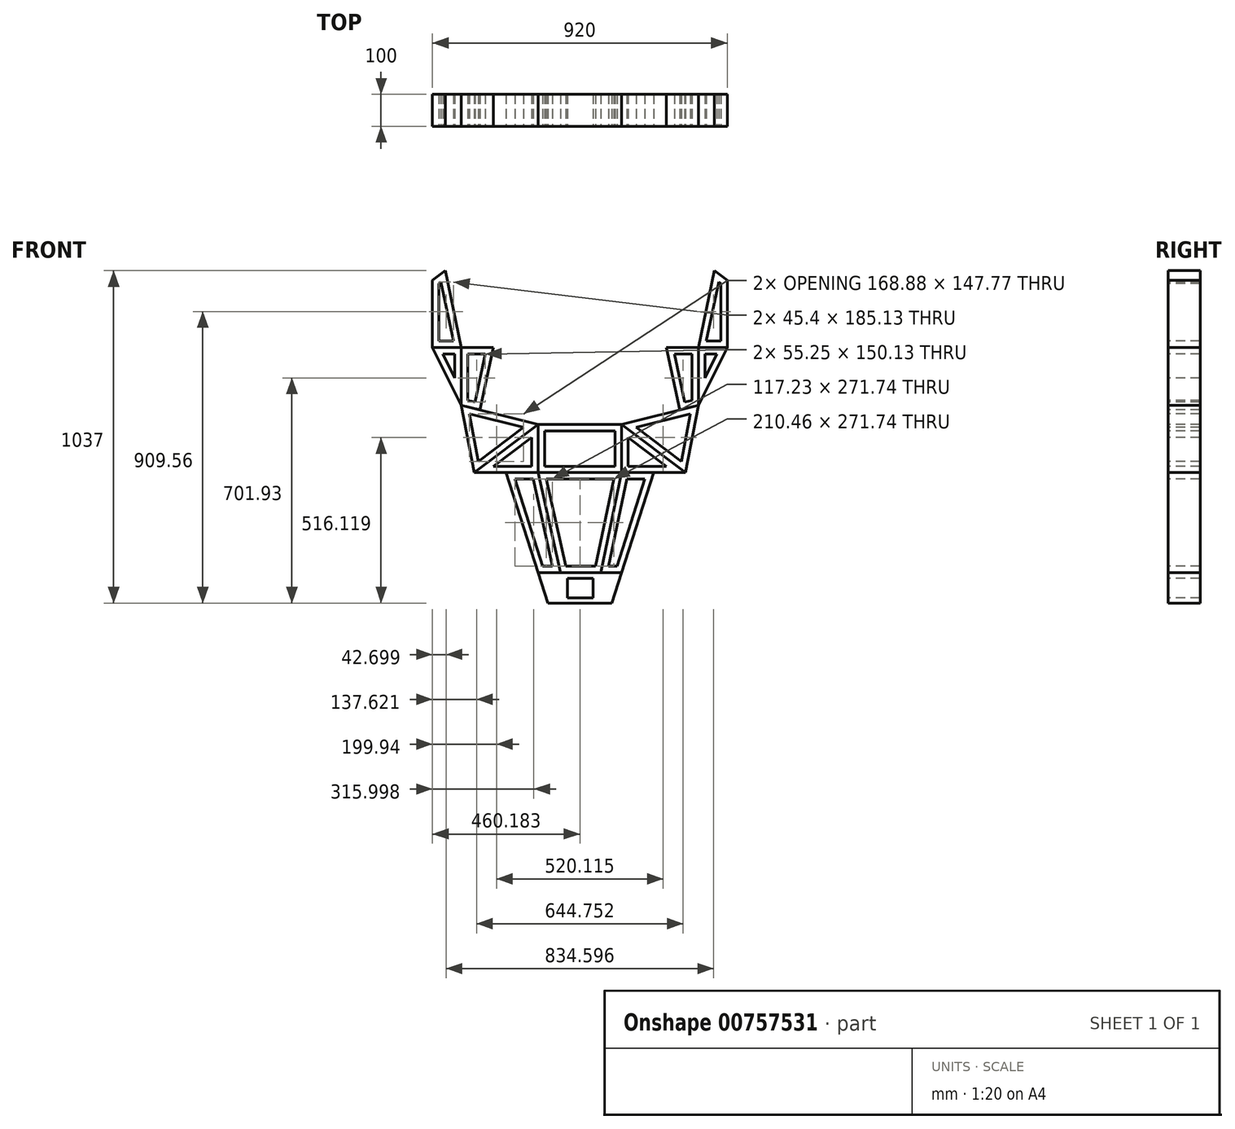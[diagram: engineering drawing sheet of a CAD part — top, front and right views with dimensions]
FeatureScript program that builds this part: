
annotation { "Feature Type Name" : "Feature", "Feature Type Description" : "" }
export const myFeature = defineFeature(function(context is Context, id is Id, definition is map)
    precondition{}
    {
        {
            var Q0;
            Q0=qCreatedBy(makeId("Top.planeOp"),FACE);
            cPlane(context, id + "F0", {"entities" : qUnion([Q0]), "cplaneType" : CPlaneType.OFFSET, "offset" : 526 * mm, "width" : 150 * mm, "height" : 150 * mm});
        }
        {
            var Q0;
            Q0=qCreatedBy(makeId("Front.planeOp"),FACE);
            var sketch = newSketch(context, id + "F1", { "sketchPlane" : qUnion([Q0])});
            skLineSegment(sketch, "E0", {"start": v(-220.81, -516.5) * mm, "end": v(-120.81, -516.5) * mm});
            skLineSegment(sketch, "E1", {"start": v(-350.81, -109.5) * mm, "end": v(-220.81, -516.5) * mm});
            skLineSegment(sketch, "E2", {"start": v(-350.81, -109.5) * mm, "end": v(-450.81, -109.5) * mm});
            skLineSegment(sketch, "E3", {"start": v(-490.81, 100.5) * mm, "end": v(-450.81, -109.5) * mm});
            skLineSegment(sketch, "E4", {"start": v(-580.81, 280.5) * mm, "end": v(-490.81, 100.5) * mm});
            skLineSegment(sketch, "E5", {"start": v(-580.81, 280.5) * mm, "end": v(-580.81, 490.5) * mm});
            skLineSegment(sketch, "E6", {"start": v(-540.81, 520.5) * mm, "end": v(-580.81, 490.5) * mm});
            skLineSegment(sketch, "E7", {"start": v(-580.81, 280.5) * mm, "end": v(-490.81, 280.5) * mm});
            skLineSegment(sketch, "E8", {"start": v(-490.81, 280.5) * mm, "end": v(-390.81, 280.5) * mm});
            skLineSegment(sketch, "E9", {"start": v(-540.81, 520.5) * mm, "end": v(-490.81, 280.5) * mm});
            skLineSegment(sketch, "E10", {"start": v(-490.81, 280.5) * mm, "end": v(-490.81, 100.5) * mm});
            skLineSegment(sketch, "E11", {"start": v(-250.81, 40.5) * mm, "end": v(-490.81, 100.5) * mm});
            skLineSegment(sketch, "E12", {"start": v(-250.81, 40.5) * mm, "end": v(-250.81, -109.5) * mm});
            skLineSegment(sketch, "E13", {"start": v(-250.81, -109.5) * mm, "end": v(-450.81, -109.5) * mm});
            skLineSegment(sketch, "E14", {"start": v(-250.81, 40.5) * mm, "end": v(-450.81, -109.5) * mm});
            skLineSegment(sketch, "E15", {"start": v(-490.81, 100.5) * mm, "end": v(-432.6, 85.95) * mm});
            skLineSegment(sketch, "E16", {"start": v(-432.6, 85.95) * mm, "end": v(-390.81, 280.5) * mm});
            skLineSegment(sketch, "E17", {"start": v(-250.81, 40.5) * mm, "end": v(-120.81, 40.5) * mm});
            skLineSegment(sketch, "E18", {"start": v(-237.82, -109.5) * mm, "end": v(-120.81, -109.5) * mm});
            skLineSegment(sketch, "E19", {"start": v(-220.81, -516.5) * mm, "end": v(-251.24, -421.23) * mm});
            skLineSegment(sketch, "E20", {"start": v(-251.24, -421.23) * mm, "end": v(-120.81, -421.23) * mm});
            skLineSegment(sketch, "E21.MirrorCS", {"start": v(249.19, 100.5) * mm, "end": v(190.98, 85.95) * mm});
            skLineSegment(sketch, "E22.MirrorCS", {"start": v(190.98, 85.95) * mm, "end": v(149.19, 280.5) * mm});
            skLineSegment(sketch, "E23.MirrorCS", {"start": v(-20.81, -516.5) * mm, "end": v(9.61, -421.23) * mm});
            skLineSegment(sketch, "E24.MirrorCS", {"start": v(9.19, 40.5) * mm, "end": v(9.19, -109.5) * mm});
            skLineSegment(sketch, "E25.MirrorCS", {"start": v(9.19, 40.5) * mm, "end": v(249.19, 100.5) * mm});
            skLineSegment(sketch, "E26.MirrorCS", {"start": v(9.19, 40.5) * mm, "end": v(209.19, -109.5) * mm});
            skLineSegment(sketch, "E27.MirrorCS", {"start": v(9.19, -109.5) * mm, "end": v(209.19, -109.5) * mm});
            skLineSegment(sketch, "E28.MirrorCS", {"start": v(109.19, -109.5) * mm, "end": v(209.19, -109.5) * mm});
            skLineSegment(sketch, "E29.MirrorCS", {"start": v(109.19, -109.5) * mm, "end": v(-20.81, -516.5) * mm});
            skLineSegment(sketch, "E30.MirrorCS", {"start": v(299.19, 520.5) * mm, "end": v(249.19, 280.5) * mm});
            skLineSegment(sketch, "E31.MirrorCS", {"start": v(339.19, 280.5) * mm, "end": v(249.19, 100.5) * mm});
            skLineSegment(sketch, "E32.MirrorCS", {"start": v(249.19, 280.5) * mm, "end": v(149.19, 280.5) * mm});
            skLineSegment(sketch, "E33.MirrorCS", {"start": v(299.19, 520.5) * mm, "end": v(339.19, 490.5) * mm});
            skLineSegment(sketch, "E34.MirrorCS", {"start": v(249.19, 280.5) * mm, "end": v(249.19, 100.5) * mm});
            skLineSegment(sketch, "E35.MirrorCS", {"start": v(339.19, 280.5) * mm, "end": v(339.19, 490.5) * mm});
            skLineSegment(sketch, "E36.MirrorCS", {"start": v(249.19, 100.5) * mm, "end": v(209.19, -109.5) * mm});
            skLineSegment(sketch, "E37.MirrorCS", {"start": v(339.19, 280.5) * mm, "end": v(249.19, 280.5) * mm});
            skLineSegment(sketch, "E38", {"start": v(-120.81, -516.5) * mm, "end": v(-20.81, -516.5) * mm});
            skLineSegment(sketch, "E39", {"start": v(-120.81, -109.5) * mm, "end": v(9.19, -109.5) * mm});
            skLineSegment(sketch, "E40", {"start": v(9.19, 40.5) * mm, "end": v(-120.81, 40.5) * mm});
            skLineSegment(sketch, "E41", {"start": v(-237.82, -109.5) * mm, "end": v(-250.81, -109.5) * mm});
            skLineSegment(sketch, "E42", {"start": v(-120.81, -421.23) * mm, "end": v(9.61, -421.23) * mm});
            skLineSegment(sketch, "E43", {"start": v(-251.24, -421.23) * mm, "end": v(-181.24, -421.23) * mm});
            skLineSegment(sketch, "E44", {"start": v(-181.24, -421.23) * mm, "end": v(-250.81, -109.5) * mm});
            skLineSegment(sketch, "E45", {"start": v(9.61, -421.23) * mm, "end": v(-55.6, -421.23) * mm});
            skLineSegment(sketch, "E46", {"start": v(9.19, -109.5) * mm, "end": v(-55.6, -421.23) * mm});
            skLineSegment(sketch, "E47.bottom", {"start": v(-160, -439.9) * mm, "end": v(-80, -439.9) * mm});
            skLineSegment(sketch, "E47.top", {"start": v(-160, -499.9) * mm, "end": v(-80, -499.9) * mm});
            skLineSegment(sketch, "E47.left", {"start": v(-160, -439.9) * mm, "end": v(-160, -499.9) * mm});
            skLineSegment(sketch, "E47.right", {"start": v(-80, -439.9) * mm, "end": v(-80, -499.9) * mm});
            skSolve(sketch);
        }
        {
            var Q0;
            Q0=makeQuery(id+"F1.imprint","IMPRINT",FACE,{"disambiguationData":[TD([[makeQuery(id+"F1.imprint","IMPRINT",EDGE,{"derivedFrom":sQuery(id+"F1.wireOp",EDGE,"E5")}),-1.0]])]});
            var Q1;
            Q1=makeQuery(id+"F1.imprint","IMPRINT",FACE,{"disambiguationData":[TD([[makeQuery(id+"F1.imprint","IMPRINT",EDGE,{"derivedFrom":sQuery(id+"F1.wireOp",EDGE,"E8")}),-1.0]])]});
            var Q2;
            {var subQ0=sQuery(id+"F1.wireOp",EDGE,"E12");Q2=makeQuery(id+"F1.imprint","IMPRINT",FACE,{"disambiguationData":[TD([[makeQuery(id+"F1.imprint","IMPRINT",EDGE,{"derivedFrom":subQ0}),-1.0]])]});}
            var Q3;
            {var subQ2=sQuery(id+"F1.wireOp",EDGE,"E26.MirrorCS");Q3=makeQuery(id+"F1.imprint","IMPRINT",FACE,{"disambiguationData":[TD([[makeQuery(id+"F1.imprint","IMPRINT",EDGE,{"derivedFrom":subQ2}),1.0]])]});}
            var Q4;
            Q4=makeQuery(id+"F1.imprint","IMPRINT",FACE,{"disambiguationData":[TD([[makeQuery(id+"F1.imprint","IMPRINT",EDGE,{"derivedFrom":sQuery(id+"F1.wireOp",EDGE,"E31.MirrorCS")}),-1.0]])]});
            var Q5;
            {var subQ1=sQuery(id+"F1.wireOp",EDGE,"E18");Q5=makeQuery(id+"F1.imprint","IMPRINT",FACE,{"disambiguationData":[TD([[makeQuery(id+"F1.imprint","IMPRINT",EDGE,{"derivedFrom":subQ1}),-1.0]])]});}
            extrude(context, id + "F2", {"entities" : qUnion([Q0, Q1, Q2, Q3, Q4, Q5]), "oppositeDirection" : true, "depth" : 100 * mm, "offsetDistance" : 25 * mm});
        }
        {
            var Q0;
            Q0=makeQuery(id+"F2.opExtrude","CAP_FACE",FACE,{"disambiguationData":[OSD([sQuery(id+"F1.wireOp",EDGE,"E5"),sQuery(id+"F1.wireOp",EDGE,"E6"),sQuery(id+"F1.wireOp",EDGE,"E7"),sQuery(id+"F1.wireOp",EDGE,"E9")])],"isStart":false});
            var Q1;
            Q1=makeQuery(id+"F2.opExtrude","CAP_FACE",FACE,{"disambiguationData":[OSD([sQuery(id+"F1.wireOp",EDGE,"E8"),sQuery(id+"F1.wireOp",EDGE,"E10"),sQuery(id+"F1.wireOp",EDGE,"E15"),sQuery(id+"F1.wireOp",EDGE,"E16")])],"isStart":false});
            var Q2;
            Q2=makeQuery(id+"F2.opExtrude","CAP_FACE",FACE,{"disambiguationData":[OSD([sQuery(id+"F1.wireOp",EDGE,"E5"),sQuery(id+"F1.wireOp",EDGE,"E6"),sQuery(id+"F1.wireOp",EDGE,"E7"),sQuery(id+"F1.wireOp",EDGE,"E9")])],"isStart":true});
            var Q3;
            Q3=makeQuery(id+"F2.opExtrude","CAP_FACE",FACE,{"disambiguationData":[OSD([sQuery(id+"F1.wireOp",EDGE,"E8"),sQuery(id+"F1.wireOp",EDGE,"E10"),sQuery(id+"F1.wireOp",EDGE,"E15"),sQuery(id+"F1.wireOp",EDGE,"E16")])],"isStart":true});
            var Q4;
            Q4=makeQuery(id+"F2.opExtrude","CAP_FACE",FACE,{"disambiguationData":[OSD([sQuery(id+"F1.wireOp",EDGE,"E12"),sQuery(id+"F1.wireOp",EDGE,"E13"),sQuery(id+"F1.wireOp",EDGE,"E14")])],"isStart":true});
            var Q5;
            Q5=makeQuery(id+"F2.opExtrude","CAP_FACE",FACE,{"disambiguationData":[OSD([sQuery(id+"F1.wireOp",EDGE,"E12"),sQuery(id+"F1.wireOp",EDGE,"E13"),sQuery(id+"F1.wireOp",EDGE,"E14")])],"isStart":false});
            var Q6;
            Q6=makeQuery(id+"F2.opExtrude","CAP_FACE",FACE,{"disambiguationData":[OSD([sQuery(id+"F1.wireOp",EDGE,"3vrYTysw-Djxj-waoJ-6IuY-1xZsEdksAOHA"),sQuery(id+"F1.wireOp",EDGE,"E18"),sQuery(id+"F1.wireOp",EDGE,"E20"),sQuery(id+"F1.wireOp",EDGE,"E41"),sQuery(id+"F1.wireOp",EDGE,"E44")])],"isStart":false});
            var Q7;
            Q7=makeQuery(id+"F2.opExtrude","CAP_FACE",FACE,{"disambiguationData":[OSD([sQuery(id+"F1.wireOp",EDGE,"3vrYTysw-Djxj-waoJ-6IuY-1xZsEdksAOHA"),sQuery(id+"F1.wireOp",EDGE,"E24.MirrorCS"),sQuery(id+"F1.wireOp",EDGE,"E39"),sQuery(id+"F1.wireOp",EDGE,"E40")])],"isStart":false});
            var Q8;
            Q8=makeQuery(id+"F2.opExtrude","CAP_FACE",FACE,{"disambiguationData":[OSD([sQuery(id+"F1.wireOp",EDGE,"E25.MirrorCS"),sQuery(id+"F1.wireOp",EDGE,"E26.MirrorCS"),sQuery(id+"F1.wireOp",EDGE,"E36.MirrorCS")])],"isStart":false});
            var Q9;
            Q9=makeQuery(id+"F2.opExtrude","CAP_FACE",FACE,{"disambiguationData":[OSD([sQuery(id+"F1.wireOp",EDGE,"E31.MirrorCS"),sQuery(id+"F1.wireOp",EDGE,"E34.MirrorCS"),sQuery(id+"F1.wireOp",EDGE,"E37.MirrorCS")])],"isStart":false});
            var Q10;
            Q10=makeQuery(id+"F2.opExtrude","CAP_FACE",FACE,{"disambiguationData":[OSD([sQuery(id+"F1.wireOp",EDGE,"3vrYTysw-Djxj-waoJ-6IuY-1xZsEdksAOHA"),sQuery(id+"F1.wireOp",EDGE,"E29.MirrorCS"),sQuery(id+"F1.wireOp",EDGE,"E38"),sQuery(id+"F1.wireOp",EDGE,"E42"),sQuery(id+"F1.wireOp",EDGE,"E45")])],"isStart":false});
            var Q11;
            Q11=makeQuery(id+"F2.opExtrude","CAP_FACE",FACE,{"disambiguationData":[OSD([sQuery(id+"F1.wireOp",EDGE,"3vrYTysw-Djxj-waoJ-6IuY-1xZsEdksAOHA"),sQuery(id+"F1.wireOp",EDGE,"E24.MirrorCS"),sQuery(id+"F1.wireOp",EDGE,"E39"),sQuery(id+"F1.wireOp",EDGE,"E40")])],"isStart":true});
            var Q12;
            Q12=makeQuery(id+"F2.opExtrude","CAP_FACE",FACE,{"disambiguationData":[OSD([sQuery(id+"F1.wireOp",EDGE,"3vrYTysw-Djxj-waoJ-6IuY-1xZsEdksAOHA"),sQuery(id+"F1.wireOp",EDGE,"E29.MirrorCS"),sQuery(id+"F1.wireOp",EDGE,"E38"),sQuery(id+"F1.wireOp",EDGE,"E42"),sQuery(id+"F1.wireOp",EDGE,"E45")])],"isStart":true});
            var Q13;
            Q13=makeQuery(id+"F2.opExtrude","CAP_FACE",FACE,{"disambiguationData":[OSD([sQuery(id+"F1.wireOp",EDGE,"3vrYTysw-Djxj-waoJ-6IuY-1xZsEdksAOHA"),sQuery(id+"F1.wireOp",EDGE,"E18"),sQuery(id+"F1.wireOp",EDGE,"E20"),sQuery(id+"F1.wireOp",EDGE,"E41"),sQuery(id+"F1.wireOp",EDGE,"E44")])],"isStart":true});
            var Q14;
            Q14=makeQuery(id+"F2.opExtrude","CAP_FACE",FACE,{"disambiguationData":[OSD([sQuery(id+"F1.wireOp",EDGE,"E25.MirrorCS"),sQuery(id+"F1.wireOp",EDGE,"E26.MirrorCS"),sQuery(id+"F1.wireOp",EDGE,"E36.MirrorCS")])],"isStart":true});
            var Q15;
            Q15=makeQuery(id+"F2.opExtrude","CAP_FACE",FACE,{"disambiguationData":[OSD([sQuery(id+"F1.wireOp",EDGE,"E31.MirrorCS"),sQuery(id+"F1.wireOp",EDGE,"E34.MirrorCS"),sQuery(id+"F1.wireOp",EDGE,"E37.MirrorCS")])],"isStart":true});
            shell(context, id + "F3", {"entities" : qUnion([Q0, Q1, Q2, Q3, Q4, Q5, Q6, Q7, Q8, Q9, Q10, Q11, Q12, Q13, Q14, Q15]), "thickness" : 20 * mm});
        }
        {
            var Q0;
            Q0=makeQuery(id+"F1.imprint","IMPRINT",FACE,{"disambiguationData":[TD([[makeQuery(id+"F1.imprint","IMPRINT",EDGE,{"derivedFrom":sQuery(id+"F1.wireOp",EDGE,"E4")}),1.0]])]});
            var Q1;
            Q1=makeQuery(id+"F1.imprint","IMPRINT",FACE,{"disambiguationData":[TD([[makeQuery(id+"F1.imprint","IMPRINT",EDGE,{"derivedFrom":sQuery(id+"F1.wireOp",EDGE,"E3")}),1.0]])]});
            var Q2;
            Q2=makeQuery(id+"F1.imprint","IMPRINT",FACE,{"disambiguationData":[TD([[makeQuery(id+"F1.imprint","IMPRINT",EDGE,{"derivedFrom":sQuery(id+"F1.wireOp",EDGE,"E24.MirrorCS")}),1.0]])]});
            var Q3;
            {var subQ0=sQuery(id+"F1.wireOp",EDGE,"E22.MirrorCS");Q3=makeQuery(id+"F1.imprint","IMPRINT",FACE,{"disambiguationData":[TD([[makeQuery(id+"F1.imprint","IMPRINT",EDGE,{"derivedFrom":subQ0}),-1.0]])]});}
            var Q4;
            Q4=makeQuery(id+"F1.imprint","IMPRINT",FACE,{"disambiguationData":[TD([[makeQuery(id+"F1.imprint","IMPRINT",EDGE,{"derivedFrom":sQuery(id+"F1.wireOp",EDGE,"E30.MirrorCS")}),1.0]])]});
            var Q5;
            {var subQ0=sQuery(id+"F1.wireOp",EDGE,"E1");Q5=makeQuery(id+"F1.imprint","IMPRINT",FACE,{"disambiguationData":[TD([[makeQuery(id+"F1.imprint","IMPRINT",EDGE,{"derivedFrom":subQ0}),1.0]])]});}
            extrude(context, id + "F4", {"entities" : qUnion([Q0, Q1, Q2, Q3, Q4, Q5]), "oppositeDirection" : true, "depth" : 100 * mm, "offsetDistance" : 25 * mm});
        }
        {
            var Q0;
            Q0=makeQuery(id+"F4.opExtrude","CAP_FACE",FACE,{"disambiguationData":[OSD([sQuery(id+"F1.wireOp",EDGE,"E30.MirrorCS"),sQuery(id+"F1.wireOp",EDGE,"E33.MirrorCS"),sQuery(id+"F1.wireOp",EDGE,"E35.MirrorCS"),sQuery(id+"F1.wireOp",EDGE,"E37.MirrorCS")])],"isStart":false});
            var Q1;
            Q1=makeQuery(id+"F4.opExtrude","CAP_FACE",FACE,{"disambiguationData":[OSD([sQuery(id+"F1.wireOp",EDGE,"E22.MirrorCS"),sQuery(id+"F1.wireOp",EDGE,"E25.MirrorCS"),sQuery(id+"F1.wireOp",EDGE,"E32.MirrorCS"),sQuery(id+"F1.wireOp",EDGE,"E34.MirrorCS")])],"isStart":false});
            var Q2;
            Q2=makeQuery(id+"F4.opExtrude","CAP_FACE",FACE,{"disambiguationData":[OSD([sQuery(id+"F1.wireOp",EDGE,"E24.MirrorCS"),sQuery(id+"F1.wireOp",EDGE,"E26.MirrorCS"),sQuery(id+"F1.wireOp",EDGE,"E27.MirrorCS"),sQuery(id+"F1.wireOp",EDGE,"E28.MirrorCS")])],"isStart":false});
            var Q3;
            Q3=makeQuery(id+"F4.opExtrude","CAP_FACE",FACE,{"disambiguationData":[OSD([sQuery(id+"F1.wireOp",EDGE,"E1"),sQuery(id+"F1.wireOp",EDGE,"E13"),sQuery(id+"F1.wireOp",EDGE,"E43"),sQuery(id+"F1.wireOp",EDGE,"E44")])],"isStart":false});
            var Q4;
            Q4=makeQuery(id+"F4.opExtrude","CAP_FACE",FACE,{"disambiguationData":[OSD([sQuery(id+"F1.wireOp",EDGE,"E3"),sQuery(id+"F1.wireOp",EDGE,"E11"),sQuery(id+"F1.wireOp",EDGE,"E14"),sQuery(id+"F1.wireOp",EDGE,"E15")])],"isStart":false});
            var Q5;
            Q5=makeQuery(id+"F4.opExtrude","CAP_FACE",FACE,{"disambiguationData":[OSD([sQuery(id+"F1.wireOp",EDGE,"E4"),sQuery(id+"F1.wireOp",EDGE,"E7"),sQuery(id+"F1.wireOp",EDGE,"E10")])],"isStart":false});
            var Q6;
            Q6=makeQuery(id+"F4.opExtrude","CAP_FACE",FACE,{"disambiguationData":[OSD([sQuery(id+"F1.wireOp",EDGE,"E30.MirrorCS"),sQuery(id+"F1.wireOp",EDGE,"E33.MirrorCS"),sQuery(id+"F1.wireOp",EDGE,"E35.MirrorCS"),sQuery(id+"F1.wireOp",EDGE,"E37.MirrorCS")])],"isStart":true});
            var Q7;
            Q7=makeQuery(id+"F4.opExtrude","CAP_FACE",FACE,{"disambiguationData":[OSD([sQuery(id+"F1.wireOp",EDGE,"E22.MirrorCS"),sQuery(id+"F1.wireOp",EDGE,"E25.MirrorCS"),sQuery(id+"F1.wireOp",EDGE,"E32.MirrorCS"),sQuery(id+"F1.wireOp",EDGE,"E34.MirrorCS")])],"isStart":true});
            var Q8;
            Q8=makeQuery(id+"F4.opExtrude","CAP_FACE",FACE,{"disambiguationData":[OSD([sQuery(id+"F1.wireOp",EDGE,"E24.MirrorCS"),sQuery(id+"F1.wireOp",EDGE,"E26.MirrorCS"),sQuery(id+"F1.wireOp",EDGE,"E27.MirrorCS"),sQuery(id+"F1.wireOp",EDGE,"E28.MirrorCS")])],"isStart":true});
            var Q9;
            Q9=makeQuery(id+"F4.opExtrude","CAP_FACE",FACE,{"disambiguationData":[OSD([sQuery(id+"F1.wireOp",EDGE,"E3"),sQuery(id+"F1.wireOp",EDGE,"E11"),sQuery(id+"F1.wireOp",EDGE,"E14"),sQuery(id+"F1.wireOp",EDGE,"E15")])],"isStart":true});
            var Q10;
            Q10=makeQuery(id+"F4.opExtrude","CAP_FACE",FACE,{"disambiguationData":[OSD([sQuery(id+"F1.wireOp",EDGE,"E4"),sQuery(id+"F1.wireOp",EDGE,"E7"),sQuery(id+"F1.wireOp",EDGE,"E10")])],"isStart":true});
            var Q11;
            Q11=makeQuery(id+"F4.opExtrude","CAP_FACE",FACE,{"disambiguationData":[OSD([sQuery(id+"F1.wireOp",EDGE,"E1"),sQuery(id+"F1.wireOp",EDGE,"E13"),sQuery(id+"F1.wireOp",EDGE,"E43"),sQuery(id+"F1.wireOp",EDGE,"E44")])],"isStart":true});
            shell(context, id + "F5", {"entities" : qUnion([Q0, Q1, Q2, Q3, Q4, Q5, Q6, Q7, Q8, Q9, Q10, Q11]), "thickness" : 20 * mm});
        }
        {
            var Q0;
            Q0=makeQuery(id+"F1.imprint","IMPRINT",FACE,{"disambiguationData":[TD([[makeQuery(id+"F1.imprint","IMPRINT",EDGE,{"derivedFrom":sQuery(id+"F1.wireOp",EDGE,"E0")}),1.0]])]});
            var Q1;
            Q1=makeQuery(id+"F1.imprint","IMPRINT",FACE,{"disambiguationData":[TD([[makeQuery(id+"F1.imprint","IMPRINT",EDGE,{"derivedFrom":sQuery(id+"F1.wireOp",EDGE,"E12")}),1.0]])]});
            extrude(context, id + "F6", {"entities" : qUnion([Q0, Q1]), "oppositeDirection" : true, "depth" : 100 * mm, "offsetDistance" : 25 * mm});
        }
        {
            var Q0;
            {var subQ0=sQuery(id+"F1.wireOp",EDGE,"E27.MirrorCS");Q0=makeQuery(id+"F1.imprint","IMPRINT",FACE,{"disambiguationData":[TD([[makeQuery(id+"F1.imprint","IMPRINT",EDGE,{"derivedFrom":subQ0}),-1.0]])]});}
            extrude(context, id + "F7", {"entities" : qUnion([Q0]), "oppositeDirection" : true, "depth" : 100 * mm, "offsetDistance" : 25 * mm});
        }
        {
            var Q0;
            Q0=makeQuery(id+"F7.opExtrude","CAP_FACE",FACE,{"disambiguationData":[OSD([sQuery(id+"F1.wireOp",EDGE,"E27.MirrorCS"),sQuery(id+"F1.wireOp",EDGE,"E29.MirrorCS"),sQuery(id+"F1.wireOp",EDGE,"E45"),sQuery(id+"F1.wireOp",EDGE,"E46")])],"isStart":false});
            var Q1;
            Q1=makeQuery(id+"F7.opExtrude","CAP_FACE",FACE,{"disambiguationData":[OSD([sQuery(id+"F1.wireOp",EDGE,"E27.MirrorCS"),sQuery(id+"F1.wireOp",EDGE,"E29.MirrorCS"),sQuery(id+"F1.wireOp",EDGE,"E45"),sQuery(id+"F1.wireOp",EDGE,"E46")])],"isStart":true});
            var Q2;
            Q2=makeQuery(id+"F6.opExtrude","CAP_FACE",FACE,{"disambiguationData":[OSD([sQuery(id+"F1.wireOp",EDGE,"E12"),sQuery(id+"F1.wireOp",EDGE,"E17"),sQuery(id+"F1.wireOp",EDGE,"E18"),sQuery(id+"F1.wireOp",EDGE,"E24.MirrorCS"),sQuery(id+"F1.wireOp",EDGE,"E39"),sQuery(id+"F1.wireOp",EDGE,"E40"),sQuery(id+"F1.wireOp",EDGE,"E41")])],"isStart":true});
            var Q3;
            Q3=makeQuery(id+"F6.opExtrude","CAP_FACE",FACE,{"disambiguationData":[OSD([sQuery(id+"F1.wireOp",EDGE,"E12"),sQuery(id+"F1.wireOp",EDGE,"E17"),sQuery(id+"F1.wireOp",EDGE,"E18"),sQuery(id+"F1.wireOp",EDGE,"E24.MirrorCS"),sQuery(id+"F1.wireOp",EDGE,"E39"),sQuery(id+"F1.wireOp",EDGE,"E40"),sQuery(id+"F1.wireOp",EDGE,"E41")])],"isStart":false});
            shell(context, id + "F8", {"entities" : qUnion([Q0, Q1, Q2, Q3]), "thickness" : 20 * mm});
        }
    });
